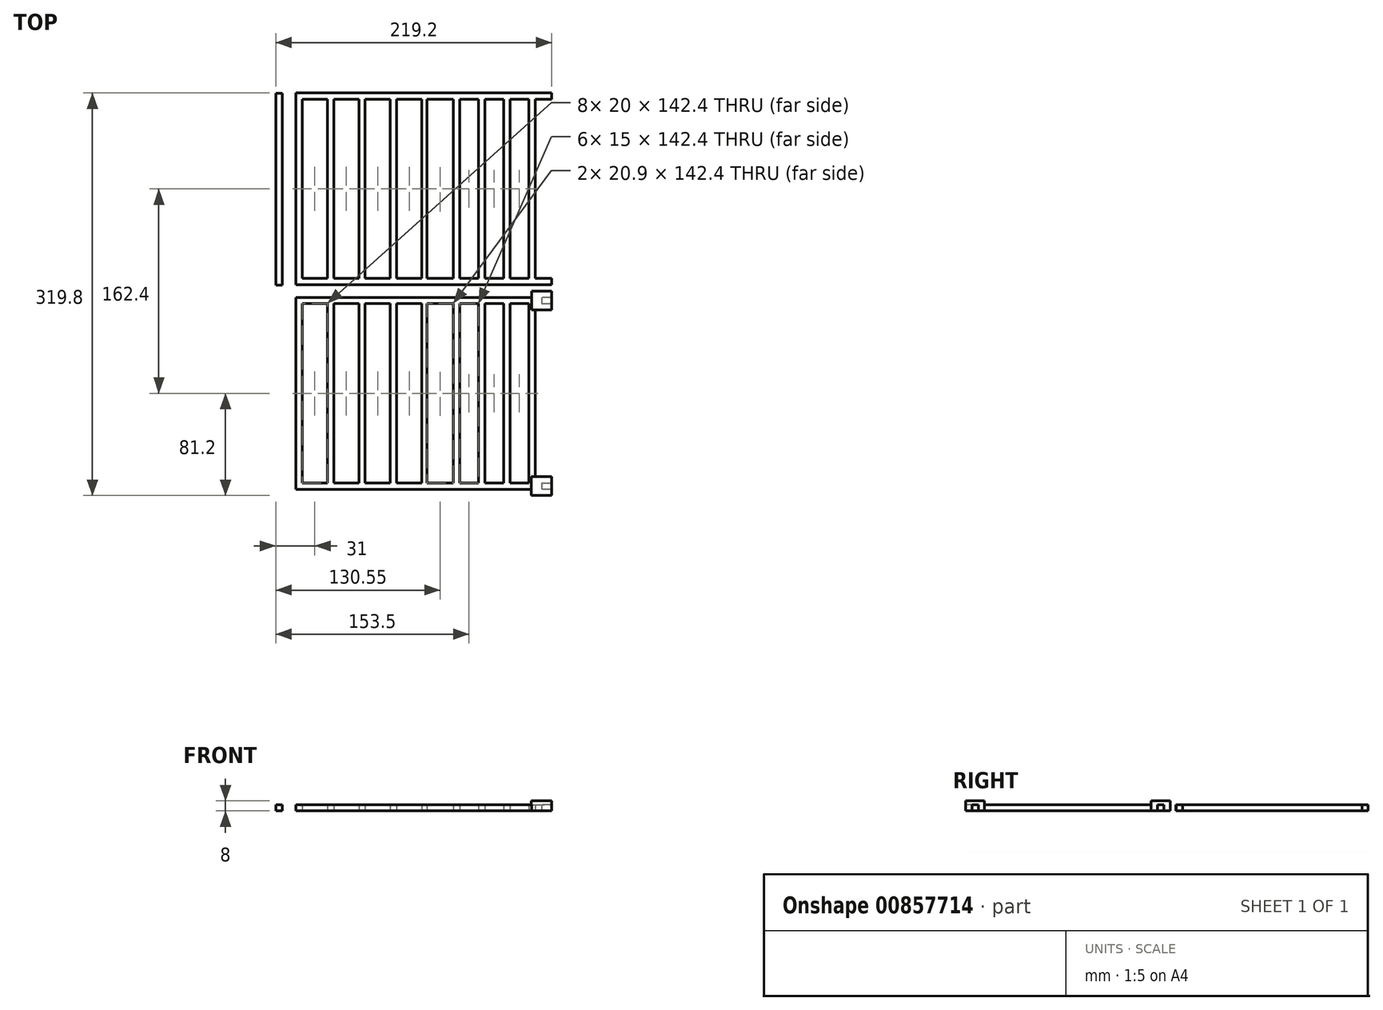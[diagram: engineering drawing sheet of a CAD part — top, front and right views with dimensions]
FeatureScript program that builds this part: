
annotation { "Feature Type Name" : "Feature", "Feature Type Description" : "" }
export const myFeature = defineFeature(function(context is Context, id is Id, definition is map)
    precondition{}
    {
        {
            var Q0;
            Q0=qCreatedBy(makeId("Top.planeOp"),FACE);
            var sketch = newSketch(context, id + "F0", { "sketchPlane" : qUnion([Q0])});
            skLineSegment(sketch, "E0", {"start": v(102.2, 76.4) * mm, "end": v(-101, 76.4) * mm});
            skLineSegment(sketch, "E1", {"start": v(-101, 76.4) * mm, "end": v(-101, -76) * mm});
            skLineSegment(sketch, "E2", {"start": v(-101, -76) * mm, "end": v(102.2, -76) * mm});
            skLineSegment(sketch, "E3", {"start": v(102.2, 76.4) * mm, "end": v(102.2, 71.4) * mm});
            skLineSegment(sketch, "E4", {"start": v(102.2, 71.4) * mm, "end": v(89, 71.4) * mm});
            skLineSegment(sketch, "E5", {"start": v(-96, 71.4) * mm, "end": v(-96, -71) * mm});
            skLineSegment(sketch, "E6", {"start": v(-96, -71) * mm, "end": v(-76, -71) * mm});
            skLineSegment(sketch, "E7", {"start": v(102.2, -71) * mm, "end": v(102.2, -76) * mm});
            skPoint(sketch, "E8", {"position": v(-76, 71.4) * mm});
            skPoint(sketch, "E9", {"position": v(-51, 71.4) * mm});
            skPoint(sketch, "E10", {"position": v(-26, 71.4) * mm});
            skPoint(sketch, "E11", {"position": v(-1, 71.4) * mm});
            skPoint(sketch, "E12", {"position": v(24, 71.4) * mm});
            skPoint(sketch, "E13", {"position": v(44, 71.4) * mm});
            skPoint(sketch, "E14", {"position": v(64, 71.4) * mm});
            skPoint(sketch, "E15", {"position": v(84, 71.4) * mm});
            skLineSegment(sketch, "E16", {"start": v(-76, 71.4) * mm, "end": v(-76, -71) * mm});
            skLineSegment(sketch, "E17", {"start": v(-71, -71) * mm, "end": v(-71, 71.4) * mm});
            skLineSegment(sketch, "E18", {"start": v(-51, 71.4) * mm, "end": v(-51, -71) * mm});
            skLineSegment(sketch, "E19", {"start": v(-46, -71) * mm, "end": v(-46, 71.4) * mm});
            skLineSegment(sketch, "E20", {"start": v(-26, 71.4) * mm, "end": v(-26, -71) * mm});
            skLineSegment(sketch, "E21", {"start": v(-21, -71) * mm, "end": v(-21, 71.4) * mm});
            skLineSegment(sketch, "E22", {"start": v(-1, 71.4) * mm, "end": v(-1, -71) * mm});
            skLineSegment(sketch, "E23", {"start": v(3.1, -71) * mm, "end": v(3.1, 71.4) * mm});
            skLineSegment(sketch, "E24.trimOffspring", {"start": v(-71, -71) * mm, "end": v(-51, -71) * mm});
            skLineSegment(sketch, "E25.trimOffspring", {"start": v(-46, -71) * mm, "end": v(-26, -71) * mm});
            skLineSegment(sketch, "E26.trimOffspring", {"start": v(-21, -71) * mm, "end": v(-1, -71) * mm});
            skLineSegment(sketch, "E27.trimOffspring", {"start": v(-26, 71.4) * mm, "end": v(-46, 71.4) * mm});
            skLineSegment(sketch, "E28.trimOffspring", {"start": v(-51, 71.4) * mm, "end": v(-71, 71.4) * mm});
            skLineSegment(sketch, "E29.trimOffspring", {"start": v(-76, 71.4) * mm, "end": v(-96, 71.4) * mm});
            skLineSegment(sketch, "E30.trimOffspring", {"start": v(3.1, -71) * mm, "end": v(24, -71) * mm});
            skLineSegment(sketch, "E31.trimOffspring", {"start": v(-1, 71.4) * mm, "end": v(-21, 71.4) * mm});
            skPoint(sketch, "E32", {"position": v(29, 71.4) * mm});
            skPoint(sketch, "E33", {"position": v(49, 71.4) * mm});
            skPoint(sketch, "E34", {"position": v(69, 71.4) * mm});
            skPoint(sketch, "E35", {"position": v(89, 71.4) * mm});
            skLineSegment(sketch, "E36", {"start": v(24, 71.4) * mm, "end": v(24, -71) * mm});
            skLineSegment(sketch, "E37", {"start": v(29, 71.4) * mm, "end": v(29, -71) * mm});
            skLineSegment(sketch, "E38", {"start": v(44, 71.4) * mm, "end": v(44, -71) * mm});
            skLineSegment(sketch, "E39", {"start": v(49, 71.4) * mm, "end": v(49, -71) * mm});
            skLineSegment(sketch, "E40", {"start": v(64, 71.4) * mm, "end": v(64, -71) * mm});
            skLineSegment(sketch, "E41", {"start": v(69, 71.4) * mm, "end": v(69, -71) * mm});
            skLineSegment(sketch, "E42", {"start": v(84, 71.4) * mm, "end": v(84, -71) * mm});
            skLineSegment(sketch, "E43", {"start": v(89, 71.4) * mm, "end": v(89, -71) * mm});
            skLineSegment(sketch, "E44", {"start": v(-162.96, -81) * mm, "end": v(94.2, -81) * mm, "construction": true});
            skLineSegment(sketch, "E45.MirrorCS", {"start": v(64, -233.4) * mm, "end": v(64, -91) * mm});
            skPoint(sketch, "E46.MirrorP", {"position": v(-1, -233.4) * mm});
            skLineSegment(sketch, "E47.MirrorCS", {"start": v(-21, -91) * mm, "end": v(-1, -91) * mm});
            skPoint(sketch, "E48.MirrorP", {"position": v(49, -233.4) * mm});
            skLineSegment(sketch, "E49.MirrorCS", {"start": v(-26, -233.4) * mm, "end": v(-26, -91) * mm});
            skLineSegment(sketch, "E50.MirrorCS", {"start": v(86.2, -238.4) * mm, "end": v(-101, -238.4) * mm});
            skLineSegment(sketch, "E51.MirrorCS", {"start": v(-21, -91) * mm, "end": v(-21, -233.4) * mm});
            skPoint(sketch, "E52.MirrorP", {"position": v(-76, -233.4) * mm});
            skLineSegment(sketch, "E53.MirrorCS", {"start": v(3.1, -91) * mm, "end": v(3.1, -233.4) * mm});
            skLineSegment(sketch, "E54.MirrorCS", {"start": v(49, -233.4) * mm, "end": v(49, -91) * mm});
            skLineSegment(sketch, "E55.MirrorCS", {"start": v(-101, -238.4) * mm, "end": v(-101, -86) * mm});
            skPoint(sketch, "E56.MirrorP", {"position": v(-51, -233.4) * mm});
            skLineSegment(sketch, "E57.MirrorCS", {"start": v(-71, -91) * mm, "end": v(-71, -233.4) * mm});
            skLineSegment(sketch, "E58.MirrorCS", {"start": v(-96, -91) * mm, "end": v(-76, -91) * mm});
            skPoint(sketch, "E59.MirrorP", {"position": v(24, -233.4) * mm});
            skLineSegment(sketch, "E60.MirrorCS", {"start": v(89, -228.4) * mm, "end": v(89, -96) * mm});
            skLineSegment(sketch, "E61.MirrorCS", {"start": v(-46, -91) * mm, "end": v(-26, -91) * mm});
            skLineSegment(sketch, "E62.MirrorCS", {"start": v(-1, -233.4) * mm, "end": v(-21, -233.4) * mm});
            skLineSegment(sketch, "E63.MirrorCS", {"start": v(-76, -233.4) * mm, "end": v(-96, -233.4) * mm});
            skLineSegment(sketch, "E64.MirrorCS", {"start": v(-76, -233.4) * mm, "end": v(-76, -91) * mm});
            skLineSegment(sketch, "E65.MirrorCS", {"start": v(-26, -233.4) * mm, "end": v(-46, -233.4) * mm});
            skPoint(sketch, "E66.MirrorP", {"position": v(-26, -233.4) * mm});
            skLineSegment(sketch, "E67.MirrorCS", {"start": v(-51, -233.4) * mm, "end": v(-51, -91) * mm});
            skLineSegment(sketch, "E68.MirrorCS", {"start": v(44, -233.4) * mm, "end": v(44, -91) * mm});
            skLineSegment(sketch, "E69.MirrorCS", {"start": v(24, -233.4) * mm, "end": v(24, -91) * mm});
            skLineSegment(sketch, "E70.MirrorCS", {"start": v(29, -233.4) * mm, "end": v(29, -91) * mm});
            skLineSegment(sketch, "E71.MirrorCS", {"start": v(-51, -233.4) * mm, "end": v(-71, -233.4) * mm});
            skLineSegment(sketch, "E72.MirrorCS", {"start": v(-46, -91) * mm, "end": v(-46, -233.4) * mm});
            skLineSegment(sketch, "E73.MirrorCS", {"start": v(69, -233.4) * mm, "end": v(69, -91) * mm});
            skPoint(sketch, "E74.MirrorP", {"position": v(29, -233.4) * mm});
            skLineSegment(sketch, "E75.MirrorCS", {"start": v(-1, -233.4) * mm, "end": v(-1, -91) * mm});
            skLineSegment(sketch, "E76.MirrorCS", {"start": v(84, -233.4) * mm, "end": v(84, -91) * mm});
            skLineSegment(sketch, "E77.MirrorCS", {"start": v(-96, -233.4) * mm, "end": v(-96, -91) * mm});
            skPoint(sketch, "E78.MirrorP", {"position": v(84, -233.4) * mm});
            skLineSegment(sketch, "E79.MirrorCS", {"start": v(3.1, -91) * mm, "end": v(24, -91) * mm});
            skPoint(sketch, "E80.MirrorP", {"position": v(64, -233.4) * mm});
            skPoint(sketch, "E81.MirrorP", {"position": v(89, -233.4) * mm});
            skLineSegment(sketch, "E82.MirrorCS", {"start": v(-71, -91) * mm, "end": v(-51, -91) * mm});
            skPoint(sketch, "E83.MirrorP", {"position": v(44, -233.4) * mm});
            skPoint(sketch, "E84.MirrorP", {"position": v(69, -233.4) * mm});
            skLineSegment(sketch, "E85.MirrorCS", {"start": v(-101, -86) * mm, "end": v(86.2, -86) * mm});
            skPoint(sketch, "E86", {"position": v(94.2, -86) * mm});
            skPoint(sketch, "E87", {"position": v(94.2, -91) * mm});
            skPoint(sketch, "E88", {"position": v(94.2, -233.4) * mm});
            skPoint(sketch, "E89", {"position": v(94.2, -238.4) * mm});
            skLineSegment(sketch, "E90.trimOffspring", {"start": v(29, -91) * mm, "end": v(44, -91) * mm});
            skLineSegment(sketch, "E91.trimOffspring", {"start": v(49, -91) * mm, "end": v(64, -91) * mm});
            skLineSegment(sketch, "E92.trimOffspring", {"start": v(69, -91) * mm, "end": v(84, -91) * mm});
            skLineSegment(sketch, "E93.trimOffspring", {"start": v(84, -233.4) * mm, "end": v(69, -233.4) * mm});
            skLineSegment(sketch, "E94.trimOffspring", {"start": v(64, -233.4) * mm, "end": v(49, -233.4) * mm});
            skLineSegment(sketch, "E95.trimOffspring", {"start": v(44, -233.4) * mm, "end": v(29, -233.4) * mm});
            skLineSegment(sketch, "E96.trimOffspring", {"start": v(24, -233.4) * mm, "end": v(3.1, -233.4) * mm});
            skLineSegment(sketch, "E97.trimOffspring", {"start": v(24, 71.4) * mm, "end": v(3.1, 71.4) * mm});
            skLineSegment(sketch, "E98.trimOffspring", {"start": v(44, 71.4) * mm, "end": v(29, 71.4) * mm});
            skLineSegment(sketch, "E99.trimOffspring", {"start": v(64, 71.4) * mm, "end": v(49, 71.4) * mm});
            skLineSegment(sketch, "E100.trimOffspring", {"start": v(84, 71.4) * mm, "end": v(69, 71.4) * mm});
            skLineSegment(sketch, "E101.trimOffspring", {"start": v(89, -71) * mm, "end": v(102.2, -71) * mm});
            skLineSegment(sketch, "E102.trimOffspring", {"start": v(69, -71) * mm, "end": v(84, -71) * mm});
            skLineSegment(sketch, "E103.trimOffspring", {"start": v(49, -71) * mm, "end": v(64, -71) * mm});
            skLineSegment(sketch, "E104.trimOffspring", {"start": v(29, -71) * mm, "end": v(44, -71) * mm});
            skLineSegment(sketch, "E105", {"start": v(94.2, -86) * mm, "end": v(94.2, -91) * mm});
            skLineSegment(sketch, "E106", {"start": v(94.2, -233.4) * mm, "end": v(94.2, -238.4) * mm});
            skPoint(sketch, "E107.right.end.orphan", {"position": v(110.2, -228.4) * mm});
            skPoint(sketch, "E108.MirrorCS.end.orphan", {"position": v(102.2, -233.4) * mm});
            skPoint(sketch, "E108.MirrorCS.start.orphan", {"position": v(102.2, -238.4) * mm});
            skPoint(sketch, "E109.top.end.orphan", {"position": v(110.2, -243.4) * mm});
            skPoint(sketch, "E110.bottom.end.orphan", {"position": v(110.2, -86) * mm});
            skLineSegment(sketch, "E111.trimOffspring", {"start": v(110.2, -81) * mm, "end": v(126, -81) * mm, "construction": true});
            skPoint(sketch, "E112.top.end.orphan", {"position": v(110.2, -96) * mm});
            skPoint(sketch, "E113.MirrorCS.end.orphan", {"position": v(102.2, -86) * mm});
            skPoint(sketch, "E113.MirrorCS.start.orphan", {"position": v(102.2, -91) * mm});
            skLineSegment(sketch, "E114.bottom", {"start": v(102.2, -86) * mm, "end": v(94.2, -86) * mm});
            skLineSegment(sketch, "E114.top", {"start": v(102.2, -81) * mm, "end": v(86.2, -81) * mm});
            skLineSegment(sketch, "E114.left", {"start": v(102.2, -86) * mm, "end": v(102.2, -81) * mm});
            skLineSegment(sketch, "E114.right", {"start": v(86.2, -86) * mm, "end": v(86.2, -81) * mm});
            skLineSegment(sketch, "E115.bottom", {"start": v(89, -96) * mm, "end": v(102.2, -96) * mm});
            skLineSegment(sketch, "E115.top", {"start": v(94.2, -91) * mm, "end": v(102.2, -91) * mm});
            skLineSegment(sketch, "E115.right", {"start": v(102.2, -96) * mm, "end": v(102.2, -91) * mm});
            skLineSegment(sketch, "E116.bottom", {"start": v(102.2, -238.4) * mm, "end": v(94.2, -238.4) * mm});
            skLineSegment(sketch, "E116.top", {"start": v(102.2, -243.4) * mm, "end": v(86.2, -243.4) * mm});
            skLineSegment(sketch, "E116.left", {"start": v(102.2, -238.4) * mm, "end": v(102.2, -243.4) * mm});
            skLineSegment(sketch, "E116.right", {"start": v(86.2, -238.4) * mm, "end": v(86.2, -243.4) * mm});
            skLineSegment(sketch, "E117.bottom", {"start": v(89, -228.4) * mm, "end": v(102.2, -228.4) * mm});
            skLineSegment(sketch, "E117.top", {"start": v(94.2, -233.4) * mm, "end": v(102.2, -233.4) * mm});
            skLineSegment(sketch, "E117.right", {"start": v(102.2, -228.4) * mm, "end": v(102.2, -233.4) * mm});
            skPoint(sketch, "E118.orphan", {"position": v(89, -91) * mm});
            skSolve(sketch);
        }
        {
            var Q0;
            Q0 = qSketchRegion(id + "F0", true);
            extrude(context, id + "F1", {"entities" : qUnion([Q0]), "depth" : 5 * mm, "offsetDistance" : 25 * mm});
        }
        {
            var Q0;
            Q0=makeQuery(id+"F1.opExtrude","CAP_FACE",FACE,{"disambiguationData":[OSD([sQuery(id+"F0.wireOp",EDGE,"E108.MirrorCS"),sQuery(id+"F0.wireOp",EDGE,"E113.MirrorCS"),sQuery(id+"F0.wireOp",EDGE,"E45.MirrorCS"),sQuery(id+"F0.wireOp",EDGE,"E47.MirrorCS"),sQuery(id+"F0.wireOp",EDGE,"E49.MirrorCS"),sQuery(id+"F0.wireOp",EDGE,"E50.MirrorCS"),sQuery(id+"F0.wireOp",EDGE,"E51.MirrorCS"),sQuery(id+"F0.wireOp",EDGE,"E53.MirrorCS"),sQuery(id+"F0.wireOp",EDGE,"E54.MirrorCS"),sQuery(id+"F0.wireOp",EDGE,"E55.MirrorCS"),sQuery(id+"F0.wireOp",EDGE,"E57.MirrorCS"),sQuery(id+"F0.wireOp",EDGE,"E58.MirrorCS"),sQuery(id+"F0.wireOp",EDGE,"E60.MirrorCS"),sQuery(id+"F0.wireOp",EDGE,"E61.MirrorCS"),sQuery(id+"F0.wireOp",EDGE,"E62.MirrorCS"),sQuery(id+"F0.wireOp",EDGE,"E63.MirrorCS"),sQuery(id+"F0.wireOp",EDGE,"E64.MirrorCS"),sQuery(id+"F0.wireOp",EDGE,"E65.MirrorCS"),sQuery(id+"F0.wireOp",EDGE,"E67.MirrorCS"),sQuery(id+"F0.wireOp",EDGE,"E68.MirrorCS"),sQuery(id+"F0.wireOp",EDGE,"E69.MirrorCS"),sQuery(id+"F0.wireOp",EDGE,"E70.MirrorCS"),sQuery(id+"F0.wireOp",EDGE,"E71.MirrorCS"),sQuery(id+"F0.wireOp",EDGE,"E72.MirrorCS"),sQuery(id+"F0.wireOp",EDGE,"E73.MirrorCS"),sQuery(id+"F0.wireOp",EDGE,"E462.MirrorCS"),sQuery(id+"F0.wireOp",EDGE,"E75.MirrorCS"),sQuery(id+"F0.wireOp",EDGE,"E76.MirrorCS"),sQuery(id+"F0.wireOp",EDGE,"E77.MirrorCS"),sQuery(id+"F0.wireOp",EDGE,"E79.MirrorCS"),sQuery(id+"F0.wireOp",EDGE,"E82.MirrorCS"),sQuery(id+"F0.wireOp",EDGE,"E85.MirrorCS"),sQuery(id+"F0.wireOp",EDGE,"E110.bottom"),sQuery(id+"F0.wireOp",EDGE,"E110.top"),sQuery(id+"F0.wireOp",EDGE,"E110.left"),sQuery(id+"F0.wireOp",EDGE,"E110.right"),sQuery(id+"F0.wireOp",EDGE,"E112.bottom"),sQuery(id+"F0.wireOp",EDGE,"E112.top"),sQuery(id+"F0.wireOp",EDGE,"E112.left"),sQuery(id+"F0.wireOp",EDGE,"E112.right"),sQuery(id+"F0.wireOp",EDGE,"E107.bottom"),sQuery(id+"F0.wireOp",EDGE,"E107.top"),sQuery(id+"F0.wireOp",EDGE,"E107.left"),sQuery(id+"F0.wireOp",EDGE,"E107.right"),sQuery(id+"F0.wireOp",EDGE,"E109.bottom"),sQuery(id+"F0.wireOp",EDGE,"E109.top"),sQuery(id+"F0.wireOp",EDGE,"E109.left"),sQuery(id+"F0.wireOp",EDGE,"E109.right"),sQuery(id+"F0.wireOp",EDGE,"E90.trimOffspring"),sQuery(id+"F0.wireOp",EDGE,"E91.trimOffspring"),sQuery(id+"F0.wireOp",EDGE,"E92.trimOffspring"),sQuery(id+"F0.wireOp",EDGE,"90a64e95-a5bb-4b1c-b3ff-9088f7b7c7f7.trimOffspring"),sQuery(id+"F0.wireOp",EDGE,"E93.trimOffspring"),sQuery(id+"F0.wireOp",EDGE,"E94.trimOffspring"),sQuery(id+"F0.wireOp",EDGE,"E95.trimOffspring"),sQuery(id+"F0.wireOp",EDGE,"E96.trimOffspring")])],"isStart":false});
            var sketch = newSketch(context, id + "F2", { "sketchPlane" : qUnion([Q0])});
            skLineSegment(sketch, "E119.bottom", {"start": v(86.2, -81) * mm, "end": v(102.2, -81) * mm});
            skLineSegment(sketch, "E119.top", {"start": v(86.2, -96) * mm, "end": v(102.2, -96) * mm});
            skLineSegment(sketch, "E119.left", {"start": v(86.2, -81) * mm, "end": v(86.2, -96) * mm});
            skLineSegment(sketch, "E119.right", {"start": v(102.2, -81) * mm, "end": v(102.2, -96) * mm});
            skLineSegment(sketch, "E120.bottom", {"start": v(86.05, -228.4) * mm, "end": v(102.2, -228.4) * mm});
            skLineSegment(sketch, "E120.top", {"start": v(86.05, -243.4) * mm, "end": v(102.2, -243.4) * mm});
            skLineSegment(sketch, "E120.left", {"start": v(86.05, -228.4) * mm, "end": v(86.05, -243.4) * mm});
            skLineSegment(sketch, "E120.right", {"start": v(102.2, -228.4) * mm, "end": v(102.2, -243.4) * mm});
            skSolve(sketch);
        }
        {
            var Q0;
            Q0 = qSketchRegion(id + "F2", true);
            extrude(context, id + "F3", {"entities" : qUnion([Q0]), "operationType" : NewBodyOperationType.ADD, "depth" : 3 * mm, "offsetDistance" : 25 * mm});
        }
        {
            var Q0;
            Q0=qCreatedBy(makeId("Top.planeOp"),FACE);
            var sketch = newSketch(context, id + "F4", { "sketchPlane" : qUnion([Q0])});
            skLineSegment(sketch, "E121.bottom", {"start": v(-117, 76) * mm, "end": v(-112, 76) * mm});
            skLineSegment(sketch, "E121.top", {"start": v(-117, -76.4) * mm, "end": v(-112, -76.4) * mm});
            skLineSegment(sketch, "E121.left", {"start": v(-117, 76) * mm, "end": v(-117, -76.4) * mm});
            skLineSegment(sketch, "E121.right", {"start": v(-112, 76) * mm, "end": v(-112, -76.4) * mm});
            skSolve(sketch);
        }
        {
            var Q0;
            Q0 = qSketchRegion(id + "F4", true);
            extrude(context, id + "F5", {"entities" : qUnion([Q0]), "depth" : 5 * mm, "offsetDistance" : 25 * mm});
        }
    });
